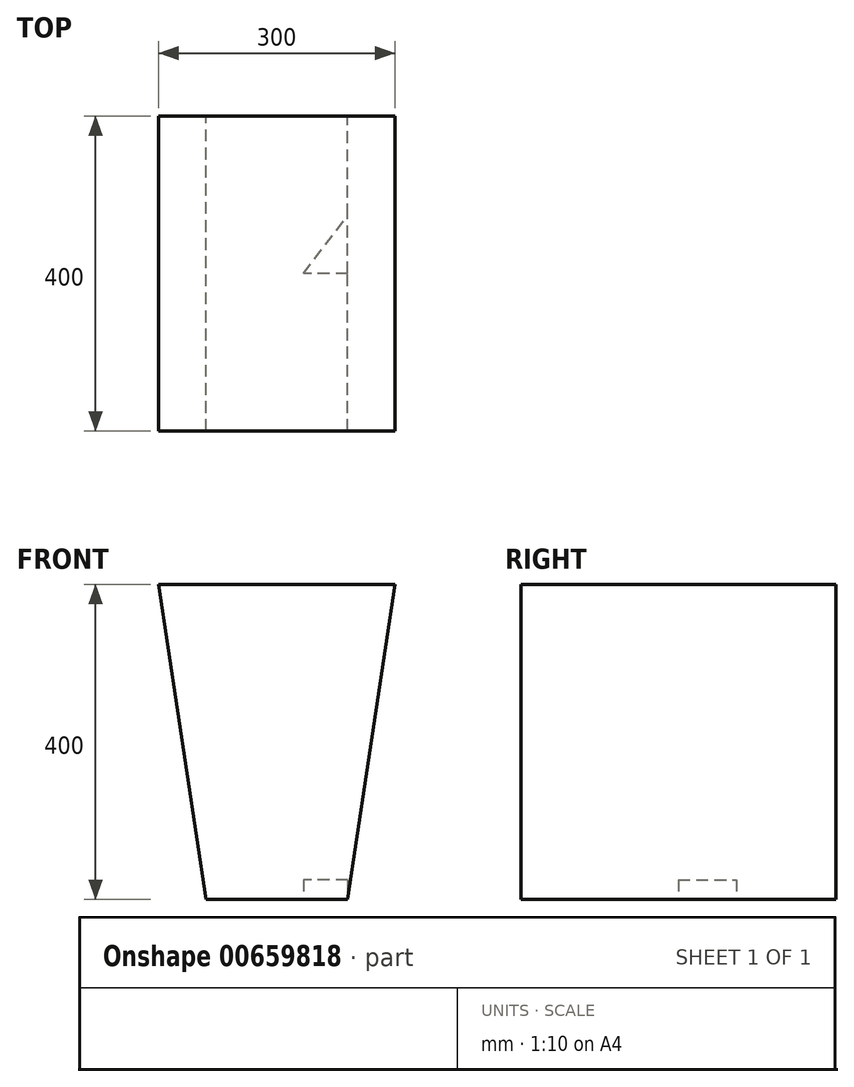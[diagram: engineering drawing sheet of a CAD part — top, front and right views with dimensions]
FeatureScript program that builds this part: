
annotation { "Feature Type Name" : "Feature", "Feature Type Description" : "" }
export const myFeature = defineFeature(function(context is Context, id is Id, definition is map)
    precondition{}
    {
        {
            var Q0;
            Q0=qCreatedBy(makeId("Front.planeOp"),FACE);
            var sketch = newSketch(context, id + "F0", { "sketchPlane" : qUnion([Q0])});
            skLineSegment(sketch, "E0", {"start": v(-90, 0) * mm, "end": v(90, 0) * mm});
            skLineSegment(sketch, "E1", {"start": v(90, 0) * mm, "end": v(150, 400) * mm});
            skLineSegment(sketch, "E2", {"start": v(150, 400) * mm, "end": v(-150, 400) * mm});
            skLineSegment(sketch, "E3", {"start": v(-150, 400) * mm, "end": v(-90, 0) * mm});
            skSolve(sketch);
        }
        {
            var Q0;
            Q0 = qSketchRegion(id + "F0", true);
            extrude(context, id + "F1", {"entities" : qUnion([Q0]), "depth" : 400 * mm, "offsetDistance" : 25 * mm});
        }
        {
            var Q0;
            Q0=makeQuery(id+"F1.opExtrude","SWEPT_FACE",FACE,{"disambiguationData":[OSD([sQuery(id+"F0.wireOp",EDGE,"E0")])]});
            var sketch = newSketch(context, id + "F2", { "sketchPlane" : qUnion([Q0])});
            skLineSegment(sketch, "E4", {"start": v(90, 200) * mm, "end": v(33.84, 200) * mm});
            skLineSegment(sketch, "E5", {"start": v(33.84, 200) * mm, "end": v(90, 126.21) * mm});
            skLineSegment(sketch, "E6", {"start": v(90, 126.21) * mm, "end": v(90, 200) * mm});
            skSolve(sketch);
        }
        {
            var Q0;
            Q0 = qSketchRegion(id + "F2", true);
            extrude(context, id + "F3", {"entities" : qUnion([Q0]), "operationType" : NewBodyOperationType.REMOVE, "oppositeDirection" : true, "depth" : 25 * mm, "offsetDistance" : 25 * mm});
        }
    });
